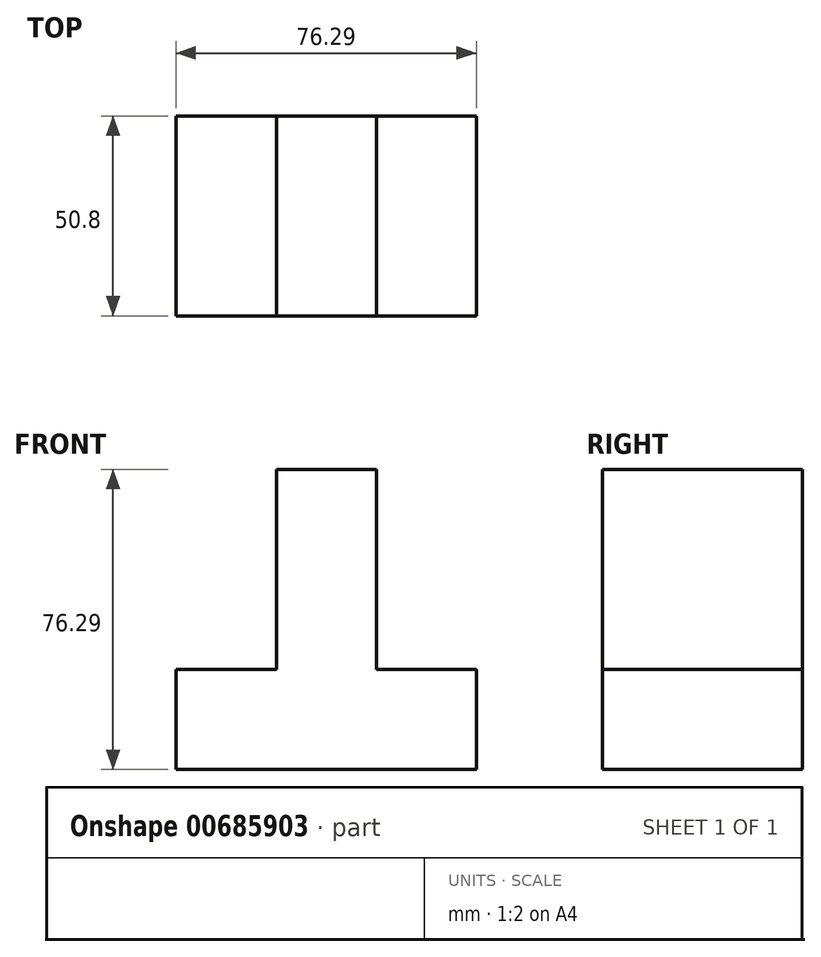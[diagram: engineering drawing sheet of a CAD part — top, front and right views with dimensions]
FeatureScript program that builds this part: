
annotation { "Feature Type Name" : "Feature", "Feature Type Description" : "" }
export const myFeature = defineFeature(function(context is Context, id is Id, definition is map)
    precondition{}
    {
        {
            var Q0;
            Q0=qCreatedBy(makeId("Front.planeOp"),FACE);
            var sketch = newSketch(context, id + "F0", { "sketchPlane" : qUnion([Q0])});
            skLineSegment(sketch, "E0", {"start": v(0, 0) * mm, "end": v(0, 25.5) * mm});
            skLineSegment(sketch, "E1", {"start": v(0, 25.5) * mm, "end": v(25.5, 25.5) * mm});
            skLineSegment(sketch, "E2", {"start": v(25.5, 25.5) * mm, "end": v(25.5, 76.29) * mm});
            skLineSegment(sketch, "E3", {"start": v(0, 0) * mm, "end": v(76.29, 0) * mm});
            skLineSegment(sketch, "E4", {"start": v(76.29, 0) * mm, "end": v(76.29, 25.5) * mm});
            skLineSegment(sketch, "E5", {"start": v(76.29, 25.5) * mm, "end": v(50.89, 25.5) * mm});
            skLineSegment(sketch, "E6", {"start": v(50.89, 25.5) * mm, "end": v(50.89, 76.29) * mm});
            skLineSegment(sketch, "E7", {"start": v(50.89, 76.29) * mm, "end": v(25.5, 76.29) * mm});
            skSolve(sketch);
        }
        {
            var Q0;
            Q0 = qSketchRegion(id + "F0", true);
            extrude(context, id + "F1", {"entities" : qUnion([Q0]), "depth" : 50.8 * mm, "offsetDistance" : 25.4 * mm});
        }
    });
